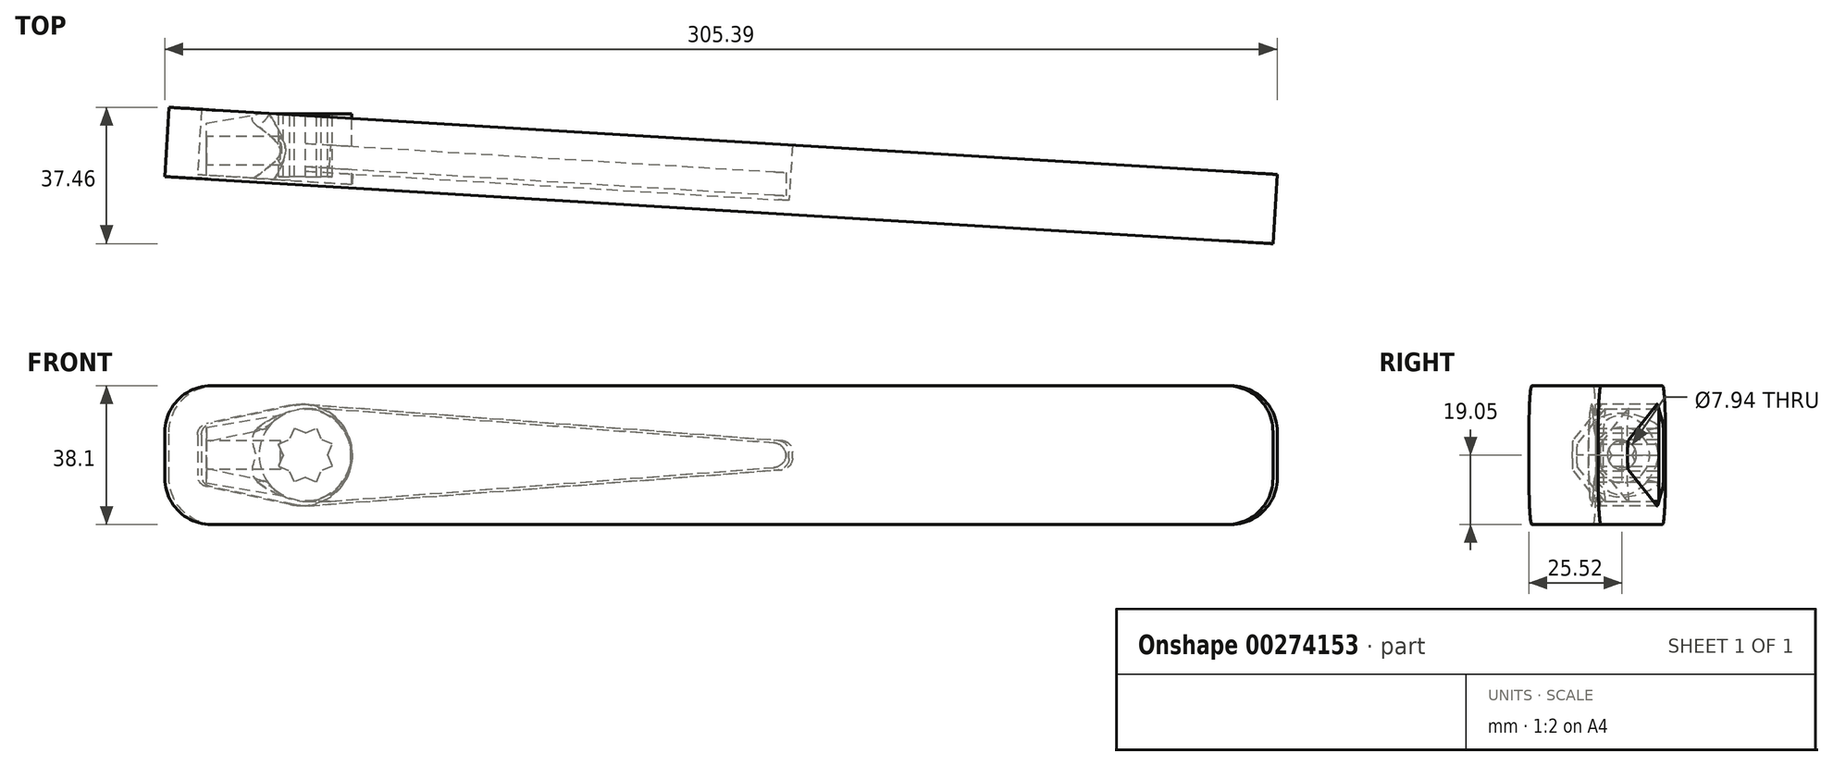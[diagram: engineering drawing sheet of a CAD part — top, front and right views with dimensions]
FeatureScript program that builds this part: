
annotation { "Feature Type Name" : "Feature", "Feature Type Description" : "" }
export const myFeature = defineFeature(function(context is Context, id is Id, definition is map)
    precondition{}
    {
        {
            var Q0;
            Q0=qCreatedBy(makeId("Front.planeOp"),FACE);
            var sketch = newSketch(context, id + "F0", { "sketchPlane" : qUnion([Q0])});
            skCircle(sketch, "E0", {"center": v(0, 0) * mm, "radius": 12.7 * mm});
            skSolve(sketch);
        }
        {
            var Q0;
            Q0=makeQuery(id+"F0.imprint","IMPRINT",FACE,{"disambiguationData":[TD([[makeQuery(id+"F0.imprint","IMPRINT",EDGE,{"derivedFrom":sQuery(id+"F0.wireOp",EDGE,"E0")}),1.0]])]});
            extrude(context, id + "F1", {"entities" : qUnion([Q0]), "depth" : 20.32 * mm});
        }
        {
            var Q0;
            Q0=qCreatedBy(makeId("Top.planeOp"),FACE);
            var sketch = newSketch(context, id + "F2", { "sketchPlane" : qUnion([Q0])});
            skLineSegment(sketch, "E1", {"start": v(0, -8.12) * mm, "end": v(132.08, -16.13) * mm});
            skLineSegment(sketch, "E2", {"start": v(132.08, -16.13) * mm, "end": v(132.08, -22.49) * mm});
            skLineSegment(sketch, "E3", {"start": v(132.08, -22.49) * mm, "end": v(0, -14.48) * mm});
            skLineSegment(sketch, "E4", {"start": v(0, -14.48) * mm, "end": v(0, -8.12) * mm});
            skLineSegment(sketch, "E5", {"start": v(12.72, 0) * mm, "end": v(12.72, -8.9) * mm, "construction": true});
            skLineSegment(sketch, "E6", {"start": v(96.52, 33.04) * mm, "end": v(96.52, -13.97) * mm, "construction": true});
            skLineSegment(sketch, "E7", {"start": v(0, 5.57) * mm, "end": v(0, -10.16) * mm});
            skLineSegment(sketch, "E8", {"start": v(23.29, -20.01) * mm, "end": v(-45.27, -15.86) * mm});
            skLineSegment(sketch, "E9", {"start": v(-45.27, -15.86) * mm, "end": v(-45.27, -25.56) * mm});
            skLineSegment(sketch, "E10", {"start": v(-45.27, -25.56) * mm, "end": v(23.29, -29.71) * mm});
            skLineSegment(sketch, "E11", {"start": v(23.29, -29.71) * mm, "end": v(23.29, -20.01) * mm});
            skLineSegment(sketch, "E12", {"start": v(-27.14, -2.54) * mm, "end": v(0, 2.04) * mm});
            skLineSegment(sketch, "E13", {"start": v(0, 2.04) * mm, "end": v(0, -10.16) * mm});
            skPoint(sketch, "E14", {"position": v(0, -11.3) * mm});
            skLineSegment(sketch, "E15", {"start": v(-27.14, -2.54) * mm, "end": v(-27.14, -10.16) * mm});
            skLineSegment(sketch, "E16", {"start": v(0, -10.16) * mm, "end": v(-27.14, -10.16) * mm});
            skSolve(sketch);
        }
        {
            var Q0;
            {var subQ3=sQuery(id+"F2.wireOp",EDGE,"E12");Q0=makeQuery(id+"F2.imprint","IMPRINT",FACE,{"disambiguationData":[TD([[makeQuery(id+"F2.imprint","IMPRINT",EDGE,{"derivedFrom":subQ3}),-1.0]])]});}
            var Q1;
            Q1=sQuery(id+"F2.wireOp",EDGE,"E16");
            revolve(context, id + "F3", {"operationType" : NewBodyOperationType.ADD, "entities" : qUnion([Q0]), "axis" : qUnion([Q1]), "revolveType" : RevolveType.FULL});
        }
        {
            var Q0;
            Q0=makeQuery(id+"F2.imprint","IMPRINT",FACE,{"disambiguationData":[TD([[makeQuery(id+"F2.imprint","IMPRINT",EDGE,{"derivedFrom":sQuery(id+"F2.wireOp",EDGE,"E8")}),1.0]])]});
            extrude(context, id + "F4", {"entities" : qUnion([Q0]), "operationType" : NewBodyOperationType.REMOVE, "endBound" : BoundingType.THROUGH_ALL, "depth" : 25.4 * mm, "hasSecondDirection" : true, "secondDirectionBound" : SecondDirectionBoundingType.THROUGH_ALL, "secondDirectionOppositeDirection" : true, "secondDirectionDepth" : 25.4 * mm});
        }
        {
            var Q0;
            Q0=makeQuery(id+"F1.opExtrude","CAP_FACE",FACE,{"disambiguationData":[OSD([sQuery(id+"F0.wireOp",EDGE,"E0")])],"isStart":true});
            var sketch = newSketch(context, id + "F5", { "sketchPlane" : qUnion([Q0])});
            skLineSegment(sketch, "E17.bottom", {"start": v(30.58, -26.89) * mm, "end": v(-36.78, -26.89) * mm});
            skLineSegment(sketch, "E17.top", {"start": v(30.58, 27.49) * mm, "end": v(-36.78, 27.49) * mm});
            skLineSegment(sketch, "E17.left", {"start": v(30.58, -26.89) * mm, "end": v(30.58, 27.49) * mm});
            skLineSegment(sketch, "E17.right", {"start": v(-36.78, -26.89) * mm, "end": v(-36.78, 27.49) * mm});
            skSolve(sketch);
        }
        {
            var Q0;
            Q0 = qSketchRegion(id + "F5", true);
            extrude(context, id + "F6", {"entities" : qUnion([Q0]), "operationType" : NewBodyOperationType.REMOVE, "endBound" : BoundingType.THROUGH_ALL, "depth" : 25.4 * mm});
        }
        {
            var Q0;
            Q0=makeQuery(id+"F2.imprint","IMPRINT",FACE,{"disambiguationData":[TD([[makeQuery(id+"F2.imprint","IMPRINT",EDGE,{"derivedFrom":sQuery(id+"F2.wireOp",EDGE,"E1")}),-1.0]])]});
            extrude(context, id + "F7", {"entities" : qUnion([Q0]), "operationType" : NewBodyOperationType.ADD, "endBound" : BoundingType.SYMMETRIC, "depth" : 25.4 * mm});
        }
        {
            var Q0;
            Q0=makeQuery(id+"F7.opExtrude","SWEPT_FACE",FACE,{"disambiguationData":[OSD([sQuery(id+"F2.wireOp",EDGE,"E1")])]});
            var sketch = newSketch(context, id + "F8", { "sketchPlane" : qUnion([Q0])});
            skLineSegment(sketch, "E18", {"start": v(-7.55, 12.7) * mm, "end": v(-139.13, 2.7) * mm});
            skLineSegment(sketch, "E19", {"start": v(-139.13, 2.7) * mm, "end": v(-140.72, 23.55) * mm});
            skLineSegment(sketch, "E20", {"start": v(-140.72, 23.55) * mm, "end": v(-7.55, 12.7) * mm});
            skLineSegment(sketch, "E21.MirrorCS", {"start": v(-7.55, -12.7) * mm, "end": v(-139.13, -2.7) * mm});
            skLineSegment(sketch, "E22.MirrorCS", {"start": v(-139.13, -2.7) * mm, "end": v(-140.72, -23.55) * mm});
            skLineSegment(sketch, "E23.MirrorCS", {"start": v(-140.72, -23.55) * mm, "end": v(-7.55, -12.7) * mm});
            skLineSegment(sketch, "E24", {"start": v(-132.81, -3.17) * mm, "end": v(-132.81, 3.17) * mm, "construction": true});
            skSolve(sketch);
        }
        {
            var Q0;
            {var subQ6=sQuery(id+"F8.wireOp",EDGE,"E19");Q0=makeQuery(id+"F8.imprint","IMPRINT",FACE,{"disambiguationData":[TD([[makeQuery(id+"F8.imprint","IMPRINT",EDGE,{"derivedFrom":subQ6}),-1.0]])]});}
            var Q1;
            {var subQ0=sQuery(id+"F8.wireOp",EDGE,"E18");var subQ1=sQuery(id+"F2.wireOp",EDGE,"E1");var subQ2=makeQuery(id+"F7.opExtrude","CAP_EDGE",EDGE,{"disambiguationData":[OSD([subQ1])],"isStart":false});var subQ3=makeQuery(id+"F8.imprint","INTERSECT",VERTEX,{"derivedFrom":[subQ2,subQ0,sQuery(id+"F8.wireOp",EDGE,"E20")]});Q1=makeQuery(id+"F8.imprint","IMPRINT",FACE,{"disambiguationData":[TD([[makeQuery(id+"F8.imprint","IMPRINT",EDGE,{"disambiguationData":[TD([[subQ3,-1.0]])],"derivedFrom":subQ0}),-1.0]])]});}
            var Q2;
            {var subQ0=sQuery(id+"F8.wireOp",EDGE,"E21.MirrorCS");var subQ1=sQuery(id+"F2.wireOp",EDGE,"E1");var subQ2=makeQuery(id+"F7.opExtrude","CAP_EDGE",EDGE,{"disambiguationData":[OSD([subQ1])],"isStart":true});var subQ3=makeQuery(id+"F8.imprint","INTERSECT",VERTEX,{"derivedFrom":[subQ2,subQ0,sQuery(id+"F8.wireOp",EDGE,"E23.MirrorCS")]});Q2=makeQuery(id+"F8.imprint","IMPRINT",FACE,{"disambiguationData":[TD([[makeQuery(id+"F8.imprint","IMPRINT",EDGE,{"disambiguationData":[TD([[subQ3,-1.0]])],"derivedFrom":subQ0}),1.0]])]});}
            var Q3;
            {var subQ7=sQuery(id+"F8.wireOp",EDGE,"E22.MirrorCS");Q3=makeQuery(id+"F8.imprint","IMPRINT",FACE,{"disambiguationData":[TD([[makeQuery(id+"F8.imprint","IMPRINT",EDGE,{"derivedFrom":subQ7}),1.0]])]});}
            var Q4;
            Q4=makeQuery(id+"F7.opExtrude","SWEPT_FACE",FACE,{"disambiguationData":[OSD([sQuery(id+"F2.wireOp",EDGE,"E3")])]});
            extrude(context, id + "F9", {"entities" : qUnion([Q0, Q1, Q2, Q3]), "operationType" : NewBodyOperationType.REMOVE, "endBound" : BoundingType.UP_TO_SURFACE, "oppositeDirection" : true, "endBoundEntityFace" : qUnion([Q4]), "depth" : 25.4 * mm});
        }
        {
            var Q0;
            Q0=makeQuery(id+"F1.opExtrude","CAP_FACE",FACE,{"disambiguationData":[OSD([sQuery(id+"F0.wireOp",EDGE,"E0")])],"isStart":true});
            var sketch = newSketch(context, id + "F10", { "sketchPlane" : qUnion([Q0])});
            skLineSegment(sketch, "E25", {"start": v(7.37, -3.05) * mm, "end": v(4.32, -4.32) * mm});
            skLineSegment(sketch, "E26", {"start": v(-3.05, -7.37) * mm, "end": v(-4.32, -4.32) * mm});
            skLineSegment(sketch, "E27", {"start": v(-7.37, 3.05) * mm, "end": v(-4.32, 4.32) * mm});
            skLineSegment(sketch, "E28", {"start": v(3.05, 7.37) * mm, "end": v(4.32, 4.32) * mm});
            skLineSegment(sketch, "E29.MirrorCS", {"start": v(3.05, -7.37) * mm, "end": v(4.32, -4.32) * mm});
            skLineSegment(sketch, "E30.MirrorCS", {"start": v(7.37, 3.05) * mm, "end": v(4.32, 4.32) * mm});
            skLineSegment(sketch, "E31.MirrorCS", {"start": v(-7.37, -3.05) * mm, "end": v(-4.32, -4.32) * mm});
            skLineSegment(sketch, "E32.MirrorCS", {"start": v(-3.05, 7.37) * mm, "end": v(-4.32, 4.32) * mm});
            skLineSegment(sketch, "E33.trimOffspring", {"start": v(0, -6.1) * mm, "end": v(-3.05, -7.37) * mm});
            skLineSegment(sketch, "E34.trimOffspring", {"start": v(6.1, 0) * mm, "end": v(7.37, 3.05) * mm});
            skLineSegment(sketch, "E35.trimOffspring", {"start": v(6.1, 0) * mm, "end": v(7.37, -3.05) * mm});
            skLineSegment(sketch, "E36.trimOffspring", {"start": v(0, 6.1) * mm, "end": v(-3.05, 7.37) * mm});
            skLineSegment(sketch, "E37.trimOffspring", {"start": v(0, 6.1) * mm, "end": v(3.05, 7.37) * mm});
            skLineSegment(sketch, "E38.trimOffspring", {"start": v(-6.1, 0) * mm, "end": v(-7.37, -3.05) * mm});
            skLineSegment(sketch, "E39.trimOffspring", {"start": v(-6.1, 0) * mm, "end": v(-7.37, 3.05) * mm});
            skLineSegment(sketch, "E40.trimOffspring", {"start": v(0, -6.1) * mm, "end": v(3.05, -7.37) * mm});
            skSolve(sketch);
        }
        {
            var Q0;
            Q0=makeQuery(id+"F10.imprint","IMPRINT",FACE,{"disambiguationData":[TD([[makeQuery(id+"F10.imprint","IMPRINT",EDGE,{"derivedFrom":sQuery(id+"F10.wireOp",EDGE,"E25")}),-1.0]])]});
            extrude(context, id + "F11", {"entities" : qUnion([Q0]), "operationType" : NewBodyOperationType.REMOVE, "oppositeDirection" : true, "depth" : 17.27 * mm});
        }
        {
            var Q0;
            Q0=makeQuery(id+"F3.opRevolve","SWEPT_FACE",FACE,{"disambiguationData":[OSD([sQuery(id+"F2.wireOp",EDGE,"E15")])]});
            var sketch = newSketch(context, id + "F12", { "sketchPlane" : qUnion([Q0])});
            skPoint(sketch, "E41", {"position": v(10.16, 0) * mm});
            skSolve(sketch);
        }
        {
            var Q0;
            Q0=sQuery(id+"F12.wireOp",VERTEX,"E41");
            var Q1;
            Q1=makeQuery(id+"F1.opExtrude","SWEPT_BODY",BODY,{"disambiguationData":[OSD([sQuery(id+"F0.wireOp",EDGE,"E0")])]});
            hole(context, id + "F13", {"style" : HoleStyle.SIMPLE, "endStyle" : HoleEndStyle.BLIND, "standardTappedOrClearance" : lookupTablePath({ "standard" : "ANSI", "engagement" : "75%", "pitch" : "16 tpi", "size" : "3/8", "type" : "Tapped" }), "standardBlindInLast" : lookupTablePath({ "standard" : "ANSI", "engagement" : "75%", "pitch" : "16 tpi", "size" : "3/8", "type" : "Tapped" }), "holeDiameter" : 7.94 * mm, "showTappedDepth" : true, "holeDepth" : 20.32 * mm, "tappedDepth" : 15.56 * mm, "tapClearance" : 3, "startFromSketch" : true, "locations" : qUnion([Q0]), "scope" : qUnion([Q1]), "majorDiameter" : 9.53 * mm});
        }
        {
            var Q0;
            Q0=makeQuery(id+"F7.opExtrude","SWEPT_FACE",FACE,{"disambiguationData":[OSD([sQuery(id+"F2.wireOp",EDGE,"E1")])]});
            var sketch = newSketch(context, id + "F14", { "sketchPlane" : qUnion([Q0])});
            skArc(sketch, "E42", {"start": v(2.95, 13.65) * mm, "mid": v(-13.97, 0) * mm, "end": v(2.95, -13.65) * mm});
            skLineSegment(sketch, "E43", {"start": v(2.95, -13.65) * mm, "end": v(26.02, -8.67) * mm});
            skLineSegment(sketch, "E44", {"start": v(28.53, -5.57) * mm, "end": v(28.53, 0) * mm});
            skLineSegment(sketch, "E45", {"start": v(-1.06, -13.93) * mm, "end": v(-131.1, -4.03) * mm});
            skLineSegment(sketch, "E46", {"start": v(-134.03, -0.87) * mm, "end": v(-134.03, 0) * mm});
            skLineSegment(sketch, "E47.MirrorCS", {"start": v(28.53, 5.57) * mm, "end": v(28.53, 0) * mm});
            skLineSegment(sketch, "E48.MirrorCS", {"start": v(2.95, 13.65) * mm, "end": v(26.02, 8.67) * mm});
            skLineSegment(sketch, "E49.MirrorCS", {"start": v(-1.06, 13.93) * mm, "end": v(-131.1, 4.03) * mm});
            skLineSegment(sketch, "E50.MirrorCS", {"start": v(-134.03, 0.87) * mm, "end": v(-134.03, 0) * mm});
            skLineSegment(sketch, "E51.bottom", {"start": v(37.42, -19.05) * mm, "end": v(-267.38, -19.05) * mm});
            skLineSegment(sketch, "E51.top", {"start": v(37.42, 19.05) * mm, "end": v(-267.38, 19.05) * mm});
            skLineSegment(sketch, "E51.left", {"start": v(37.42, -19.05) * mm, "end": v(37.42, 19.05) * mm});
            skLineSegment(sketch, "E51.right", {"start": v(-267.38, -19.05) * mm, "end": v(-267.38, 19.05) * mm});
            skPoint(sketch, "E52.visualSharp", {"position": v(28.53, -8.13) * mm});
            skArc(sketch, "E52.filletArc", {"start": v(26.02, -8.67) * mm, "mid": v(27.82, -7.56) * mm, "end": v(28.53, -5.57) * mm});
            skPoint(sketch, "E53.visualSharp", {"position": v(28.53, 8.13) * mm});
            skArc(sketch, "E53.filletArc", {"start": v(28.53, 5.57) * mm, "mid": v(27.82, 7.56) * mm, "end": v(26.02, 8.67) * mm});
            skPoint(sketch, "E54.visualSharp", {"position": v(-134.03, -3.81) * mm});
            skArc(sketch, "E54.filletArc", {"start": v(-134.03, -0.87) * mm, "mid": v(-133.19, -3.03) * mm, "end": v(-131.1, -4.03) * mm});
            skPoint(sketch, "E55.visualSharp", {"position": v(-134.03, 3.81) * mm});
            skArc(sketch, "E55.filletArc", {"start": v(-131.1, 4.03) * mm, "mid": v(-133.19, 3.03) * mm, "end": v(-134.03, 0.87) * mm});
            skSolve(sketch);
        }
        {
            var Q0;
            Q0=makeQuery(id+"F3.boolean.opBoolean","INTERSECT",EDGE,{"derivedFrom":[makeQuery(id+"F1.opExtrude","SWEPT_FACE",FACE,{"disambiguationData":[OSD([sQuery(id+"F0.wireOp",EDGE,"E0")])]}),makeQuery(id+"F3.opRevolve","SWEPT_FACE",FACE,{"disambiguationData":[OSD([sQuery(id+"F2.wireOp",EDGE,"E12")])]})]});
            fillet(context, id + "F15", {"entities" : qUnion([Q0]), "radius" : 5.08 * mm, "tangentPropagation" : true, "allowEdgeOverflow" : false});
        }
        {
            var Q0;
            Q0=makeQuery(id+"F9.boolean.opBoolean","INTERSECT",EDGE,{"derivedFrom":[makeQuery(id+"F7.opExtrude","SWEPT_FACE",FACE,{"disambiguationData":[OSD([sQuery(id+"F2.wireOp",EDGE,"E2")])]}),makeQuery(id+"F9.opExtrude","SWEPT_FACE",FACE,{"disambiguationData":[OSD([sQuery(id+"F8.wireOp",EDGE,"E18")])]})]});
            var Q1;
            Q1=makeQuery(id+"F9.boolean.opBoolean","INTERSECT",EDGE,{"derivedFrom":[makeQuery(id+"F7.opExtrude","SWEPT_FACE",FACE,{"disambiguationData":[OSD([sQuery(id+"F2.wireOp",EDGE,"E2")])]}),makeQuery(id+"F9.opExtrude","SWEPT_FACE",FACE,{"disambiguationData":[OSD([sQuery(id+"F8.wireOp",EDGE,"E21.MirrorCS")])]})]});
            fillet(context, id + "F16", {"entities" : qUnion([Q0, Q1]), "radius" : 3.8 * mm, "tangentPropagation" : true, "allowEdgeOverflow" : false});
        }
        {
            var Q0;
            {var subQ2=sQuery(id+"F14.wireOp",EDGE,"E43");Q0=makeQuery(id+"F14.imprint","IMPRINT",FACE,{"disambiguationData":[TD([[makeQuery(id+"F14.imprint","IMPRINT",EDGE,{"derivedFrom":subQ2}),-1.0]])]});}
            extrude(context, id + "F17", {"entities" : qUnion([Q0]), "depth" : 7.62 * mm, "hasSecondDirection" : true, "secondDirectionOppositeDirection" : true, "secondDirectionDepth" : 11.43 * mm});
        }
        {
            var Q0;
            Q0=makeQuery(id+"F17.opExtrude","CAP_FACE",FACE,{"disambiguationData":[OSD([sQuery(id+"F14.wireOp",EDGE,"E42"),sQuery(id+"F14.wireOp",EDGE,"E43"),sQuery(id+"F14.wireOp",EDGE,"E44"),sQuery(id+"F14.wireOp",EDGE,"E45"),sQuery(id+"F14.wireOp",EDGE,"E46"),sQuery(id+"F14.wireOp",EDGE,"E47.MirrorCS"),sQuery(id+"F14.wireOp",EDGE,"E48.MirrorCS"),sQuery(id+"F14.wireOp",EDGE,"E49.MirrorCS"),sQuery(id+"F14.wireOp",EDGE,"E50.MirrorCS"),sQuery(id+"F14.wireOp",EDGE,"E51.bottom"),sQuery(id+"F14.wireOp",EDGE,"E51.top"),sQuery(id+"F14.wireOp",EDGE,"E51.left"),sQuery(id+"F14.wireOp",EDGE,"E51.right"),sQuery(id+"F14.wireOp",EDGE,"E52.filletArc"),sQuery(id+"F14.wireOp",EDGE,"E53.filletArc"),sQuery(id+"F14.wireOp",EDGE,"E54.filletArc"),sQuery(id+"F14.wireOp",EDGE,"E55.filletArc")])],"isStart":true});
            var sketch = newSketch(context, id + "F18", { "sketchPlane" : qUnion([Q0])});
            skLineSegment(sketch, "E56.0", {"start": v(1.06, 13.93) * mm, "end": v(131.1, 4.03) * mm});
            skLineSegment(sketch, "E56.1", {"start": v(1.06, -13.93) * mm, "end": v(131.1, -4.03) * mm});
            skArc(sketch, "E56.2", {"start": v(131.1, 4.03) * mm, "mid": v(133.19, 3.03) * mm, "end": v(134.03, 0.87) * mm});
            skLineSegment(sketch, "E56.3", {"start": v(134.03, -0.87) * mm, "end": v(134.03, 0.87) * mm});
            skArc(sketch, "E56.4", {"start": v(134.03, -0.87) * mm, "mid": v(133.19, -3.03) * mm, "end": v(131.1, -4.03) * mm});
            skArc(sketch, "E57", {"start": v(1.06, -13.93) * mm, "mid": v(13.97, 0) * mm, "end": v(1.06, 13.93) * mm});
            skLineSegment(sketch, "E58.0", {"start": v(-2.95, 13.65) * mm, "end": v(-26.02, 8.67) * mm});
            skArc(sketch, "E58.1", {"start": v(-2.95, 13.65) * mm, "mid": v(-0.96, 13.94) * mm, "end": v(1.06, 13.93) * mm});
            skArc(sketch, "E58.2", {"start": v(1.06, -13.93) * mm, "mid": v(-0.96, -13.94) * mm, "end": v(-2.95, -13.65) * mm});
            skLineSegment(sketch, "E58.3", {"start": v(-2.95, -13.65) * mm, "end": v(-26.02, -8.67) * mm});
            skArc(sketch, "E58.4", {"start": v(-28.53, 5.57) * mm, "mid": v(-27.82, 7.56) * mm, "end": v(-26.02, 8.67) * mm});
            skLineSegment(sketch, "E58.5", {"start": v(-28.53, 5.57) * mm, "end": v(-28.53, -5.57) * mm});
            skArc(sketch, "E58.6", {"start": v(-26.02, -8.67) * mm, "mid": v(-27.82, -7.56) * mm, "end": v(-28.53, -5.57) * mm});
            skSolve(sketch);
        }
        {
            var Q0;
            {var subQ4=sQuery(id+"F18.wireOp",EDGE,"E56.2");Q0=makeQuery(id+"F18.imprint","IMPRINT",FACE,{"disambiguationData":[TD([[makeQuery(id+"F18.imprint","IMPRINT",EDGE,{"derivedFrom":subQ4}),-1.0]])]});}
            extrude(context, id + "F19", {"entities" : qUnion([Q0]), "operationType" : NewBodyOperationType.ADD, "oppositeDirection" : true, "depth" : 3.8 * mm});
        }
        {
            var Q0;
            Q0=makeQuery(id+"F19.boolean.opBoolean","MERGE",FACE,{"derivedFrom":[makeQuery(id+"F17.opExtrude","CAP_FACE",FACE,{"disambiguationData":[OSD([sQuery(id+"F14.wireOp",EDGE,"E42"),sQuery(id+"F14.wireOp",EDGE,"E43"),sQuery(id+"F14.wireOp",EDGE,"E44"),sQuery(id+"F14.wireOp",EDGE,"E45"),sQuery(id+"F14.wireOp",EDGE,"E46"),sQuery(id+"F14.wireOp",EDGE,"E47.MirrorCS"),sQuery(id+"F14.wireOp",EDGE,"E48.MirrorCS"),sQuery(id+"F14.wireOp",EDGE,"E49.MirrorCS"),sQuery(id+"F14.wireOp",EDGE,"E50.MirrorCS"),sQuery(id+"F14.wireOp",EDGE,"E51.bottom"),sQuery(id+"F14.wireOp",EDGE,"E51.top"),sQuery(id+"F14.wireOp",EDGE,"E51.left"),sQuery(id+"F14.wireOp",EDGE,"E51.right"),sQuery(id+"F14.wireOp",EDGE,"E52.filletArc"),sQuery(id+"F14.wireOp",EDGE,"E53.filletArc"),sQuery(id+"F14.wireOp",EDGE,"E54.filletArc"),sQuery(id+"F14.wireOp",EDGE,"E55.filletArc")])],"isStart":true}),makeQuery(id+"F19.opExtrude","CAP_FACE",FACE,{"disambiguationData":[OSD([sQuery(id+"F18.wireOp",EDGE,"E56.0"),sQuery(id+"F18.wireOp",EDGE,"E56.1"),sQuery(id+"F18.wireOp",EDGE,"E56.2"),sQuery(id+"F18.wireOp",EDGE,"E56.3"),sQuery(id+"F18.wireOp",EDGE,"E56.4"),sQuery(id+"F18.wireOp",EDGE,"E57")])],"isStart":true})]});
            var sketch = newSketch(context, id + "F20", { "sketchPlane" : qUnion([Q0])});
            skSolve(sketch);
        }
        {
            var Q0;
            {var subQ0=sQuery(id+"F14.wireOp",EDGE,"E43");Q0=makeQuery(id+"F20.imprint","IMPRINT",FACE,{"disambiguationData":[TD([[makeQuery(id+"F20.imprint","IMPRINT",EDGE,{"derivedFrom":makeQuery(id+"F17.opExtrude","CAP_EDGE",EDGE,{"disambiguationData":[OSD([subQ0])],"isStart":true})}),-1.0]])]});}
            extrude(context, id + "F21", {"entities" : qUnion([Q0]), "operationType" : NewBodyOperationType.ADD, "oppositeDirection" : true, "depth" : 1.02 * mm});
        }
        {
            var Q0;
            Q0=makeQuery(id+"F17.opExtrude","SWEPT_EDGE",EDGE,{"disambiguationData":[OSD([sQuery(id+"F14.wireOp",EDGE,"E51.bottom"),sQuery(id+"F14.wireOp",EDGE,"E51.left")])]});
            var Q1;
            Q1=makeQuery(id+"F17.opExtrude","SWEPT_EDGE",EDGE,{"disambiguationData":[OSD([sQuery(id+"F14.wireOp",EDGE,"E51.top"),sQuery(id+"F14.wireOp",EDGE,"E51.left")])]});
            var Q2;
            Q2=makeQuery(id+"F17.opExtrude","SWEPT_EDGE",EDGE,{"disambiguationData":[OSD([sQuery(id+"F14.wireOp",EDGE,"E51.top"),sQuery(id+"F14.wireOp",EDGE,"E51.right")])]});
            var Q3;
            Q3=makeQuery(id+"F17.opExtrude","SWEPT_EDGE",EDGE,{"disambiguationData":[OSD([sQuery(id+"F14.wireOp",EDGE,"E51.bottom"),sQuery(id+"F14.wireOp",EDGE,"E51.right")])]});
            fillet(context, id + "F22", {"entities" : qUnion([Q0, Q1, Q2, Q3]), "radius" : 12.7 * mm, "tangentPropagation" : true, "allowEdgeOverflow" : false});
        }
    });
